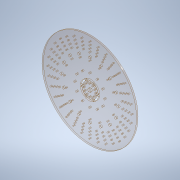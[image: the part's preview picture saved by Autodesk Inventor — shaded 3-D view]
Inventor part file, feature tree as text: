
AUTODESK INVENTOR PART (.ipt)
format: ipt  version: 2020 (Build 240168000, 168)  size: 589,824 bytes
history: native  units: in
note: dims shown in document units (in); Inventor stores cm internally (conversion verified against a paired STEP export)
features: extrude x4, sketch x4
ambient origin geometry x8: Origin, YZ Plane, XZ Plane, XY Plane, X Axis, Y Axis, Z Axis, Center Point
bodies: Solid1 (feature_tree)
feature tree (8):
  extrude  "Extrusion1"  Depth=0.25in
  extrude  "Extrusion2"  Depth=0.3937in
  extrude  "Extrusion3"  Depth=1.0in TaperAngle=0.0deg
  extrude  "Extrusion4"  Depth=0.15in
  sketch  "Sketch1"  dims[d0=0.25in d1=0.0in d2=0.2031in]
  sketch  "Sketch2"  dims[d3=5.5in d4=1.5748in d6=0.5in d7=0.3937in d9=1.0in]
  sketch  "Sketch3"  dims[d11=12.5984in d13=360.0deg d15=1.0in d16=0.0in]
  sketch  "Sketch4"  dims[d17=2.497in d18=2.0in d19=3.625in d20=0.2656in d21=4.125in d22=2.5in d23=4.7244in d25=360.0deg d27=1.0in d28=0.0in d29=0.5079in d30=0.2031in d31=0.9375in d32=4.7244in d34=360.0deg d36=0.15in d37=45.0deg d38=1.35in d39=2.3622in d41=360.0deg d43=0.0in d44=0.0in]
